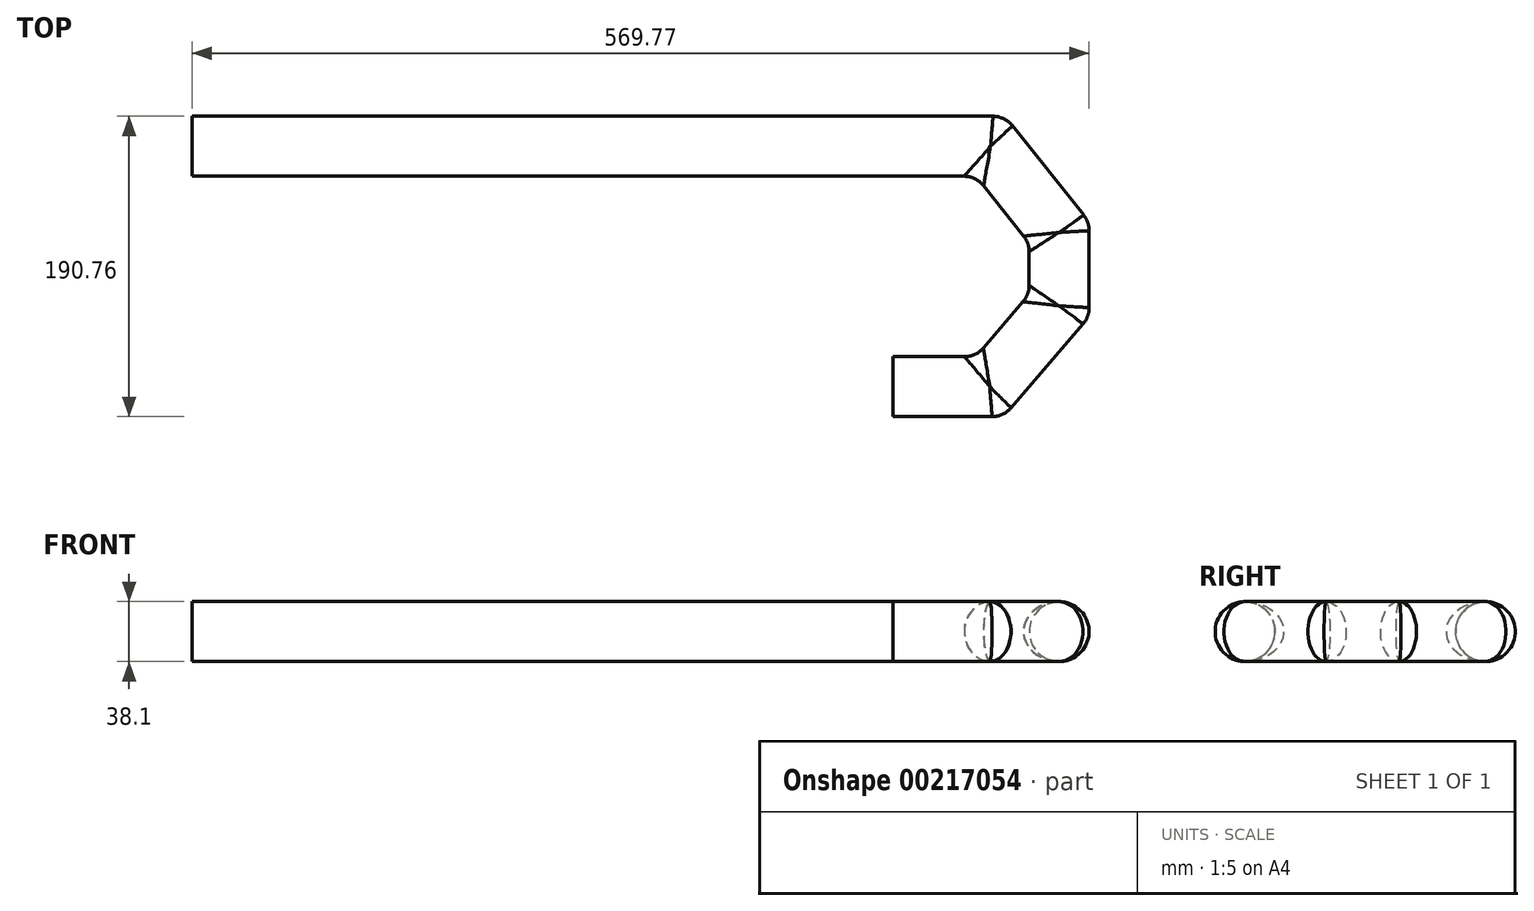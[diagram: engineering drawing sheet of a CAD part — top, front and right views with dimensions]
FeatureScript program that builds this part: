
annotation { "Feature Type Name" : "Feature", "Feature Type Description" : "" }
export const myFeature = defineFeature(function(context is Context, id is Id, definition is map)
    precondition{}
    {
        {
            var Q0;
            Q0=qCreatedBy(makeId("Top.planeOp"),FACE);
            var sketch = newSketch(context, id + "F0", { "sketchPlane" : qUnion([Q0])});
            skLineSegment(sketch, "E0", {"start": v(0, -115.52) * mm, "end": v(50.8, -115.52) * mm});
            skLineSegment(sketch, "E1", {"start": v(50.8, -115.52) * mm, "end": v(82.37, -78.73) * mm});
            skLineSegment(sketch, "E2", {"start": v(82.37, -78.73) * mm, "end": v(82.37, -48.75) * mm});
            skLineSegment(sketch, "E3", {"start": v(82.37, -48.75) * mm, "end": v(50.8, -9.06) * mm});
            skLineSegment(sketch, "E4", {"start": v(50.8, -9.06) * mm, "end": v(-366.92, -9.06) * mm});
            skLineSegment(sketch, "E5", {"start": v(-366.92, -9.06) * mm, "end": v(-394.45, -9.06) * mm});
            skSolve(sketch);
        }
        {
            var Q0;
            Q0=qCreatedBy(makeId("Right.planeOp"),FACE);
            var sketch = newSketch(context, id + "F1", { "sketchPlane" : qUnion([Q0])});
            skCircle(sketch, "E6", {"center": v(-138.62, 0) * mm, "radius": 19.05 * mm});
            skSolve(sketch);
        }
        {
            var Q0;
            Q0=makeQuery(id+"F1.imprint","IMPRINT",FACE,{"disambiguationData":[TD([[makeQuery(id+"F1.imprint","IMPRINT",EDGE,{"derivedFrom":sQuery(id+"F1.wireOp",EDGE,"E6")}),1.0]])]});
            var Q1;
            Q1=sQuery(id+"F0.wireOp",EDGE,"E0");
            var Q2;
            Q2=sQuery(id+"F0.wireOp",EDGE,"E1");
            var Q3;
            Q3=sQuery(id+"F0.wireOp",EDGE,"E2");
            var Q4;
            Q4=sQuery(id+"F0.wireOp",EDGE,"E3");
            var Q5;
            Q5=sQuery(id+"F0.wireOp",EDGE,"E4");
            var Q6;
            Q6=sQuery(id+"F0.wireOp",EDGE,"E5");
            sweep(context, id + "F2", {"profiles" : qUnion([Q0]), "path" : qUnion([Q1, Q2, Q3, Q4, Q5, Q6])});
        }
        {
            var Q0;
            Q0=makeQuery(id+"F2.opSweep","MID_CAP_EDGE",EDGE,{"disambiguationData":[OSD([sQuery(id+"F0.wireOp",VERTEX,"E4.start"),sQuery(id+"F1.wireOp",EDGE,"E6")])],"capPos":4.0});
            fillet(context, id + "F3", {"entities" : qUnion([Q0]), "radius" : 15.88 * mm, "tangentPropagation" : true, "allowEdgeOverflow" : false});
        }
        {
            var Q0;
            Q0=makeQuery(id+"F2.opSweep","MID_CAP_EDGE",EDGE,{"disambiguationData":[OSD([sQuery(id+"F0.wireOp",VERTEX,"E3.start"),sQuery(id+"F1.wireOp",EDGE,"E6")])],"capPos":3.0});
            fillet(context, id + "F4", {"entities" : qUnion([Q0]), "radius" : 15.88 * mm, "tangentPropagation" : true, "allowEdgeOverflow" : false});
        }
        {
            var Q0;
            Q0=makeQuery(id+"F2.opSweep","MID_CAP_EDGE",EDGE,{"disambiguationData":[OSD([sQuery(id+"F0.wireOp",VERTEX,"E2.start"),sQuery(id+"F1.wireOp",EDGE,"E6")])],"capPos":2.0});
            var Q1;
            Q1=makeQuery(id+"F2.opSweep","MID_CAP_EDGE",EDGE,{"disambiguationData":[OSD([sQuery(id+"F0.wireOp",VERTEX,"E1.start"),sQuery(id+"F1.wireOp",EDGE,"E6")])],"capPos":1.0});
            fillet(context, id + "F5", {"entities" : qUnion([Q0, Q1]), "radius" : 15.88 * mm, "tangentPropagation" : true, "allowEdgeOverflow" : false});
        }
        {
            var Q0;
            Q0=makeQuery(id+"F2.opSweep","CAP_FACE",FACE,{"disambiguationData":[OSD([sQuery(id+"F0.wireOp",VERTEX,"E5.end"),sQuery(id+"F1.wireOp",EDGE,"E6")])],"isStart":false});
            extrude(context, id + "F6", {"entities" : qUnion([Q0]), "operationType" : NewBodyOperationType.ADD, "depth" : 50.8 * mm});
        }
    });
